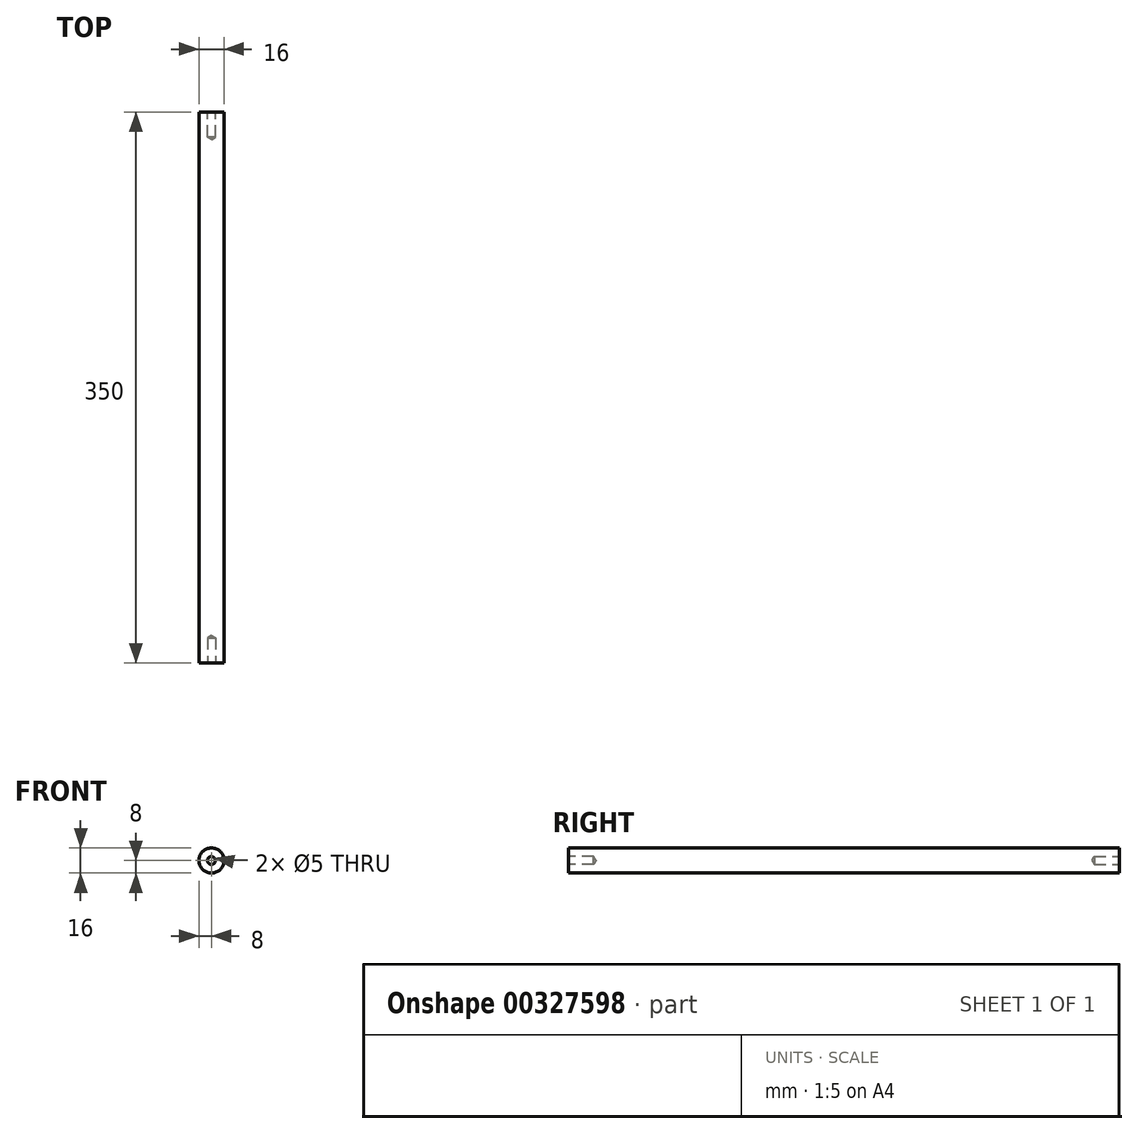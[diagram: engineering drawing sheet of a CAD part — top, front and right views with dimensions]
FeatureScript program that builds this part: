
annotation { "Feature Type Name" : "Feature", "Feature Type Description" : "" }
export const myFeature = defineFeature(function(context is Context, id is Id, definition is map)
    precondition{}
    {
        {
            var Q0;
            Q0=qCreatedBy(makeId("Front.planeOp"),FACE);
            var sketch = newSketch(context, id + "F0", { "sketchPlane" : qUnion([Q0])});
            skCircle(sketch, "E0", {"center": v(0, 0) * mm, "radius": 8 * mm});
            skLineSegment(sketch, "E1", {"start": v(0, 39.86) * mm, "end": v(0, -22.1) * mm, "construction": true});
            skLineSegment(sketch, "E2", {"start": v(0, -22.1) * mm, "end": v(44.9, 0) * mm, "construction": true});
            skLineSegment(sketch, "E3", {"start": v(44.9, 0) * mm, "end": v(-42.5, 0) * mm, "construction": true});
            skSolve(sketch);
        }
        {
            var Q0;
            Q0 = qSketchRegion(id + "F0", true);
            extrude(context, id + "F1", {"entities" : qUnion([Q0]), "depth" : 350 * mm});
        }
        {
            var Q0;
            Q0=makeQuery(id+"F1.opExtrude","CAP_FACE",FACE,{"disambiguationData":[OSD([sQuery(id+"F0.wireOp",EDGE,"E0")])],"isStart":true});
            var sketch = newSketch(context, id + "F2", { "sketchPlane" : qUnion([Q0])});
            skPoint(sketch, "E4", {"position": v(0, 0) * mm});
            skSolve(sketch);
        }
        {
            var Q0;
            Q0=makeQuery(id+"F2.imprint","IMPRINT",FACE,{"disambiguationData":[TD([[makeQuery(id+"F2.imprint","IMPRINT",EDGE,{"derivedFrom":makeQuery(id+"F1.opExtrude","CAP_EDGE",EDGE,{"disambiguationData":[OSD([sQuery(id+"F0.wireOp",EDGE,"E0")])],"isStart":true})}),-1.0]])]});
            var sketch = newSketch(context, id + "F3", { "sketchPlane" : qUnion([Q0])});
            skPoint(sketch, "E5", {"position": v(0, 0) * mm});
            skSolve(sketch);
        }
        {
            var Q0;
            Q0=sQuery(id+"F3.wireOp",VERTEX,"E5");
            var Q1;
            Q1=makeQuery(id+"F1.opExtrude","SWEPT_BODY",BODY,{"disambiguationData":[OSD([sQuery(id+"F0.wireOp",EDGE,"E0")])]});
            hole(context, id + "F4", {"style" : HoleStyle.SIMPLE, "endStyle" : HoleEndStyle.BLIND, "standardTappedOrClearance" : lookupTablePath({ "standard" : "ISO", "engagement" : "75%", "pitch" : "1 mm", "size" : "M6", "type" : "Tapped" }), "standardBlindInLast" : lookupTablePath({ "standard" : "ISO", "engagement" : "75%", "pitch" : "1 mm", "size" : "M6", "type" : "Tapped" }), "holeDiameter" : 5 * mm, "showTappedDepth" : true, "holeDepth" : 16 * mm, "tappedDepth" : 15 * mm, "tapClearance" : 1, "locations" : qUnion([Q0]), "scope" : qUnion([Q1]), "majorDiameter" : 6 * mm});
        }
        {
            var Q0;
            Q0=makeQuery(id+"F1.opExtrude","CAP_FACE",FACE,{"disambiguationData":[OSD([sQuery(id+"F0.wireOp",EDGE,"E0")])],"isStart":false});
            var sketch = newSketch(context, id + "F5", { "sketchPlane" : qUnion([Q0])});
            skPoint(sketch, "E6", {"position": v(0, 0) * mm});
            skSolve(sketch);
        }
        {
            var Q0;
            Q0=sQuery(id+"F5.wireOp",VERTEX,"E6");
            var Q1;
            Q1=makeQuery(id+"F1.opExtrude","SWEPT_BODY",BODY,{"disambiguationData":[OSD([sQuery(id+"F0.wireOp",EDGE,"E0")])]});
            hole(context, id + "F6", {"style" : HoleStyle.SIMPLE, "endStyle" : HoleEndStyle.BLIND, "standardTappedOrClearance" : lookupTablePath({ "standard" : "ISO", "engagement" : "75%", "pitch" : "1 mm", "size" : "M6", "type" : "Tapped" }), "standardBlindInLast" : lookupTablePath({ "standard" : "ISO", "engagement" : "75%", "pitch" : "1 mm", "size" : "M6", "type" : "Tapped" }), "holeDiameter" : 5 * mm, "showTappedDepth" : true, "holeDepth" : 16 * mm, "tappedDepth" : 15 * mm, "tapClearance" : 1, "locations" : qUnion([Q0]), "scope" : qUnion([Q1]), "majorDiameter" : 6 * mm});
        }
    });
